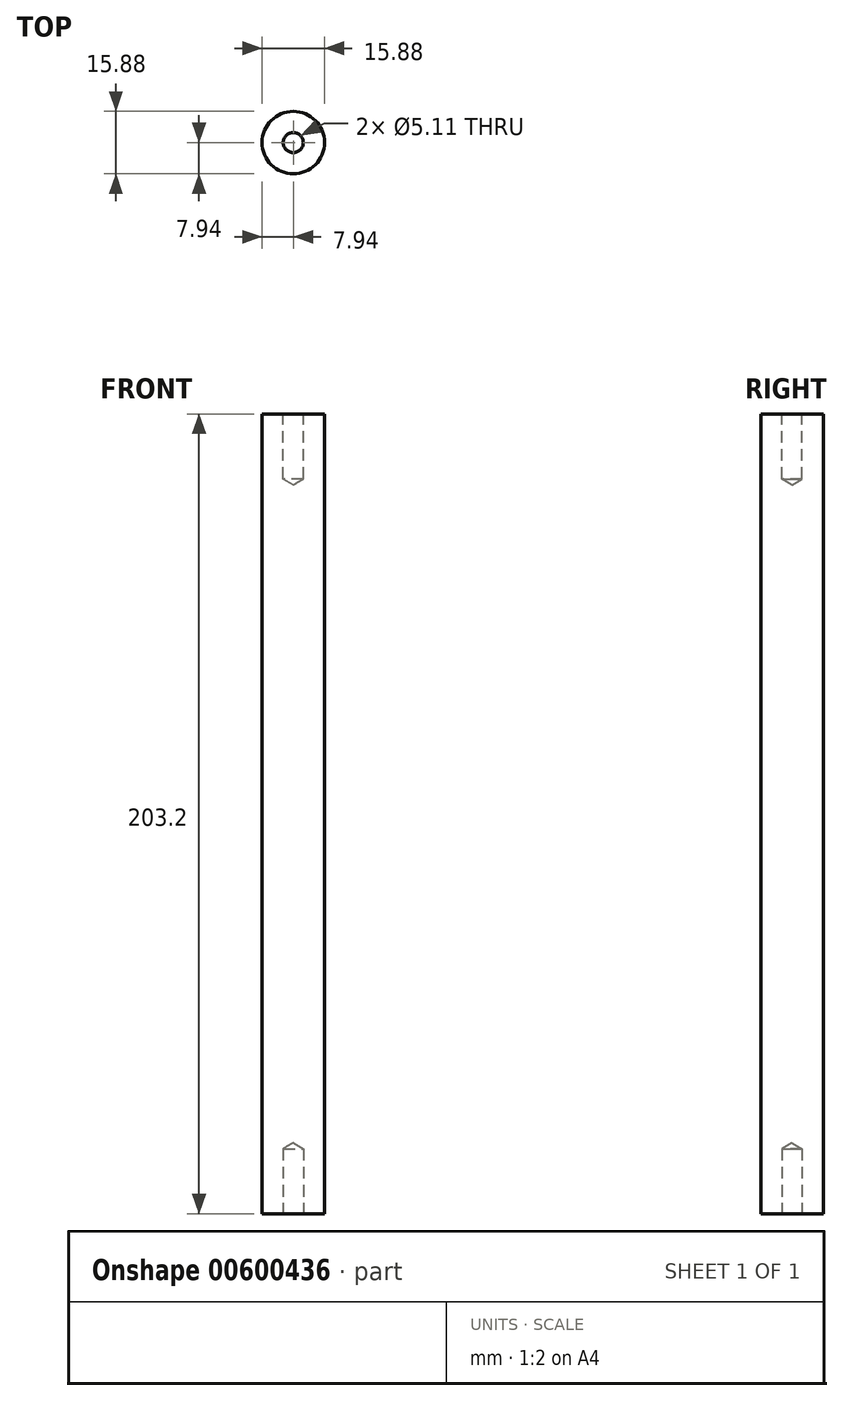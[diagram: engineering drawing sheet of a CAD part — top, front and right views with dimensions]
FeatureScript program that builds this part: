
annotation { "Feature Type Name" : "Feature", "Feature Type Description" : "" }
export const myFeature = defineFeature(function(context is Context, id is Id, definition is map)
    precondition{}
    {
        {
            var Q0;
            Q0=qCreatedBy(makeId("Top.planeOp"),FACE);
            var sketch = newSketch(context, id + "F0", { "sketchPlane" : qUnion([Q0])});
            skCircle(sketch, "E0", {"center": v(0, 0) * mm, "radius": 7.94 * mm});
            skSolve(sketch);
        }
        {
            var Q0;
            Q0 = qSketchRegion(id + "F0", true);
            extrude(context, id + "F1", {"entities" : qUnion([Q0]), "endBound" : BoundingType.SYMMETRIC, "depth" : 203.2 * mm, "offsetDistance" : 25.4 * mm});
        }
        {
            var Q0;
            Q0=makeQuery(id+"F1.opExtrude","CAP_FACE",FACE,{"disambiguationData":[OSD([sQuery(id+"F0.wireOp",EDGE,"E0")])],"isStart":false});
            var sketch = newSketch(context, id + "F2", { "sketchPlane" : qUnion([Q0])});
            skPoint(sketch, "E1", {"position": v(0, 0) * mm});
            skSolve(sketch);
        }
        {
            var Q0;
            Q0=sQuery(id+"F2.wireOp",VERTEX,"E1");
            var Q1;
            Q1=makeQuery(id+"F1.opExtrude","SWEPT_BODY",BODY,{"disambiguationData":[OSD([sQuery(id+"F0.wireOp",EDGE,"E0")])]});
            hole(context, id + "F3", {"style" : HoleStyle.SIMPLE, "endStyle" : HoleEndStyle.BLIND, "standardTappedOrClearance" : lookupTablePath({ "standard" : "ANSI", "engagement" : "75%", "pitch" : "20 tpi", "size" : "1/4", "type" : "Tapped" }), "standardBlindInLast" : lookupTablePath({ "standard" : "ANSI", "engagement" : "75%", "pitch" : "20 tpi", "size" : "1/4", "type" : "Tapped" }), "holeDiameter" : 5.1 * mm, "majorDiameter" : 6.35 * mm, "showTappedDepth" : true, "holeDepth" : 16.51 * mm, "isTappedThrough" : true, "tappedDepth" : 12.7 * mm, "tapClearance" : 3, "locations" : qUnion([Q0]), "scope" : qUnion([Q1])});
        }
        {
            var Q0;
            Q0=makeQuery(id+"F1.opExtrude","CAP_FACE",FACE,{"disambiguationData":[OSD([sQuery(id+"F0.wireOp",EDGE,"E0")])],"isStart":true});
            var sketch = newSketch(context, id + "F4", { "sketchPlane" : qUnion([Q0])});
            skPoint(sketch, "E2", {"position": v(0, 0) * mm});
            skSolve(sketch);
        }
        {
            var Q0;
            Q0=sQuery(id+"F4.wireOp",VERTEX,"E2");
            var Q1;
            Q1=makeQuery(id+"F1.opExtrude","SWEPT_BODY",BODY,{"disambiguationData":[OSD([sQuery(id+"F0.wireOp",EDGE,"E0")])]});
            hole(context, id + "F5", {"style" : HoleStyle.SIMPLE, "endStyle" : HoleEndStyle.BLIND, "standardTappedOrClearance" : lookupTablePath({ "standard" : "ANSI", "engagement" : "75%", "pitch" : "20 tpi", "size" : "1/4", "type" : "Tapped" }), "standardBlindInLast" : lookupTablePath({ "standard" : "ANSI", "engagement" : "75%", "pitch" : "20 tpi", "size" : "1/4", "type" : "Tapped" }), "holeDiameter" : 5.1 * mm, "majorDiameter" : 6.35 * mm, "showTappedDepth" : true, "holeDepth" : 16.5 * mm, "isTappedThrough" : true, "tappedDepth" : 12.7 * mm, "tapClearance" : 3, "locations" : qUnion([Q0]), "scope" : qUnion([Q1])});
        }
    });
